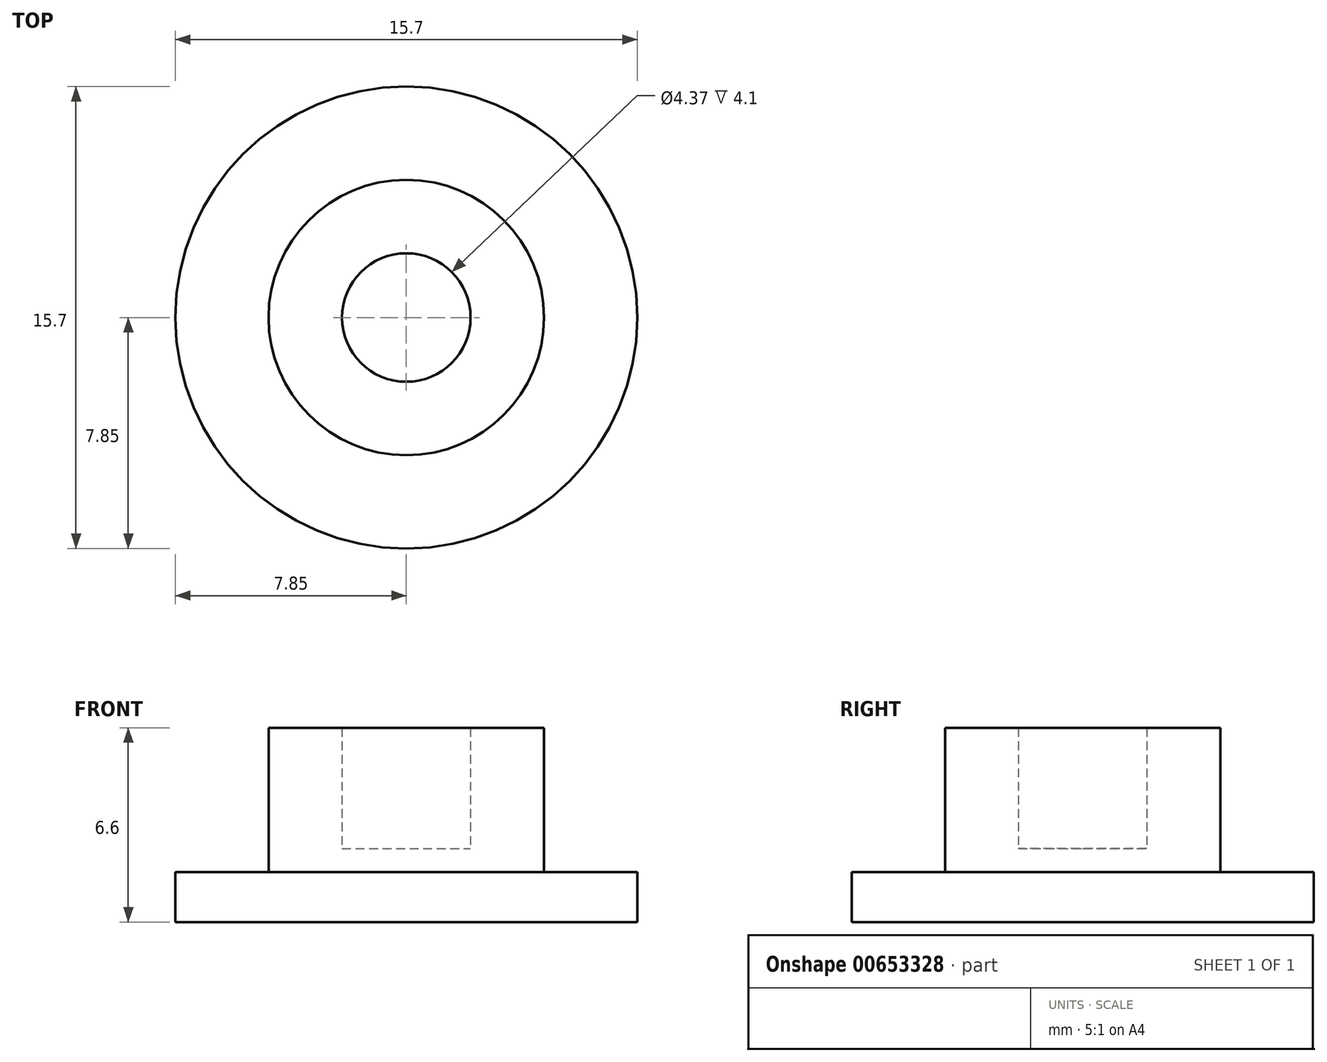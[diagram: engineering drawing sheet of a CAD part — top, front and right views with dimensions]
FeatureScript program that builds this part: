
annotation { "Feature Type Name" : "Feature", "Feature Type Description" : "" }
export const myFeature = defineFeature(function(context is Context, id is Id, definition is map)
    precondition{}
    {
        {
            var Q0;
            Q0=qCreatedBy(makeId("Top.planeOp"),FACE);
            var sketch = newSketch(context, id + "F0", { "sketchPlane" : qUnion([Q0])});
            skCircle(sketch, "E0", {"center": v(0, 0) * mm, "radius": 4.68 * mm});
            skSolve(sketch);
        }
        {
            var Q0;
            Q0 = qSketchRegion(id + "F0", true);
            extrude(context, id + "F1", {"entities" : qUnion([Q0]), "depth" : 4.9 * mm, "offsetDistance" : 25 * mm});
        }
        {
            var Q0;
            Q0=makeQuery(id+"F1.opExtrude","CAP_FACE",FACE,{"disambiguationData":[OSD([sQuery(id+"F0.wireOp",EDGE,"E0")])],"isStart":true});
            var sketch = newSketch(context, id + "F2", { "sketchPlane" : qUnion([Q0])});
            skCircle(sketch, "E1", {"center": v(0, 0) * mm, "radius": 7.85 * mm});
            skSolve(sketch);
        }
        {
            var Q0;
            Q0 = qSketchRegion(id + "F2", true);
            extrude(context, id + "F3", {"entities" : qUnion([Q0]), "operationType" : NewBodyOperationType.ADD, "depth" : 1.7 * mm, "offsetDistance" : 25 * mm});
        }
        {
            var Q0;
            Q0=makeQuery(id+"F1.opExtrude","CAP_FACE",FACE,{"disambiguationData":[OSD([sQuery(id+"F0.wireOp",EDGE,"E0")])],"isStart":false});
            var Q1;
            Q1=makeQuery(id+"F3.opExtrude","CAP_FACE",FACE,{"disambiguationData":[OSD([sQuery(id+"F2.wireOp",EDGE,"E1")])],"isStart":true});
            shell(context, id + "F4", {"entities" : qUnion([Q0, Q1]), "thickness" : 2.5 * mm});
        }
    });
